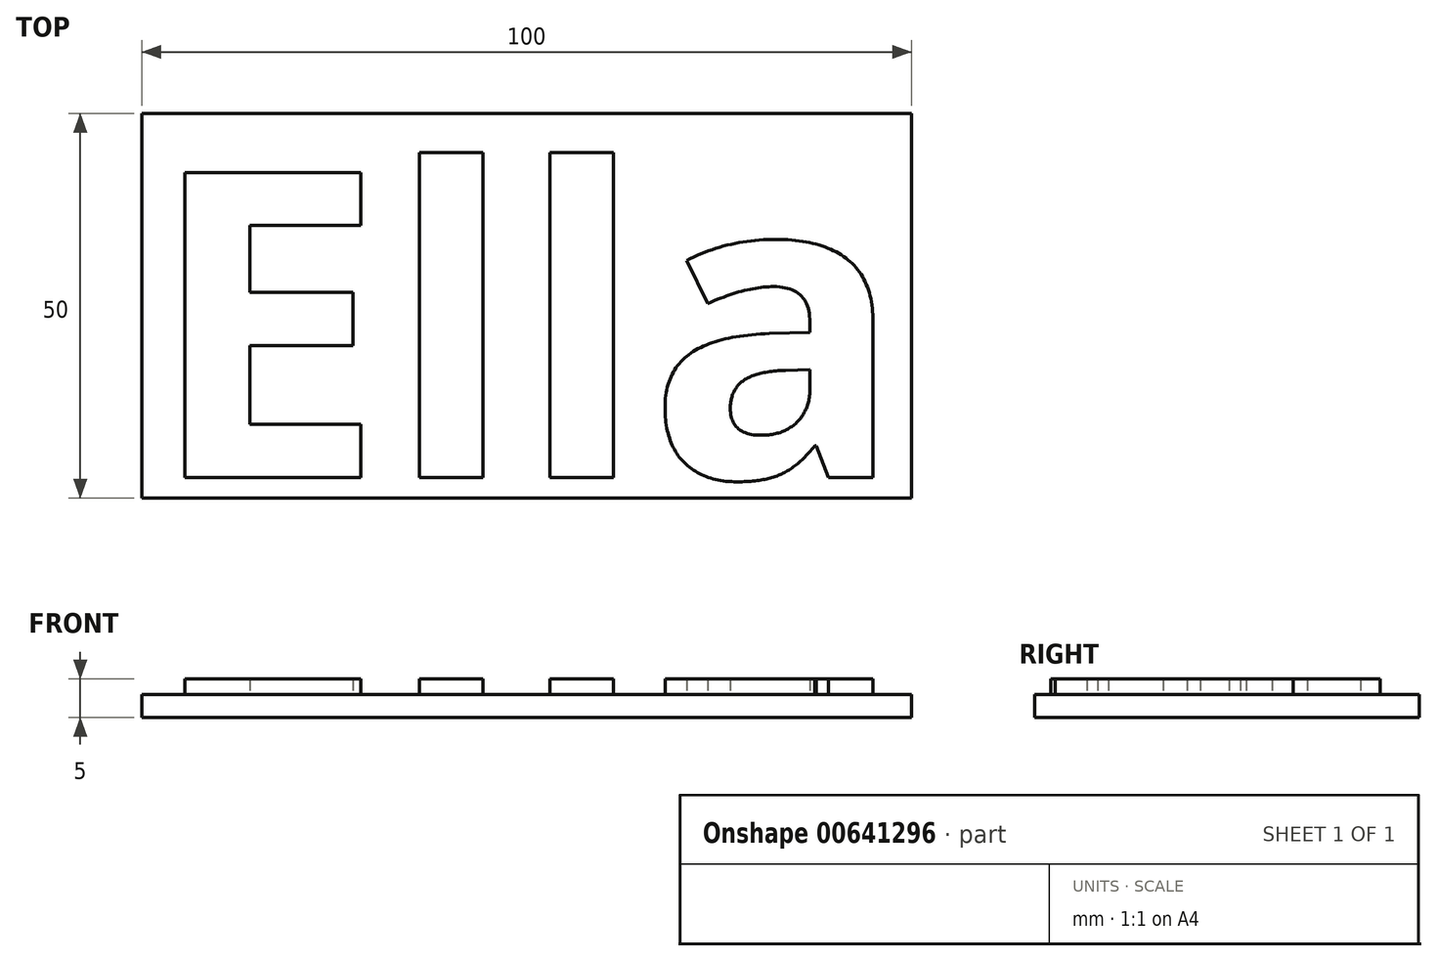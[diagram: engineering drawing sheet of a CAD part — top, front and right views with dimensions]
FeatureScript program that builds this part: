
annotation { "Feature Type Name" : "Feature", "Feature Type Description" : "" }
export const myFeature = defineFeature(function(context is Context, id is Id, definition is map)
    precondition{}
    {
        {
            var Q0;
            Q0=qCreatedBy(makeId("Top.planeOp"),FACE);
            var sketch = newSketch(context, id + "F0", { "sketchPlane" : qUnion([Q0])});
            skLineSegment(sketch, "E0.bottom", {"start": v(0, 0) * mm, "end": v(-100, 0) * mm});
            skLineSegment(sketch, "E0.top", {"start": v(0, 50) * mm, "end": v(-100, 50) * mm});
            skLineSegment(sketch, "E0.left", {"start": v(0, 0) * mm, "end": v(0, 50) * mm});
            skLineSegment(sketch, "E0.right", {"start": v(-100, 0) * mm, "end": v(-100, 50) * mm});
            skSolve(sketch);
        }
        {
            var Q0;
            Q0 = qSketchRegion(id + "F0", true);
            extrude(context, id + "F1", {"entities" : qUnion([Q0]), "depth" : 3 * mm, "offsetDistance" : 25 * mm});
        }
        {
            var Q0;
            Q0=makeQuery(id+"F1.opExtrude","CAP_FACE",FACE,{"disambiguationData":[OSD([sQuery(id+"F0.wireOp",EDGE,"E0.bottom"),sQuery(id+"F0.wireOp",EDGE,"E0.top"),sQuery(id+"F0.wireOp",EDGE,"E0.left"),sQuery(id+"F0.wireOp",EDGE,"E0.right")])],"isStart":false});
            var sketch = newSketch(context, id + "F2", { "sketchPlane" : qUnion([Q0])});
            skText(sketch, "E1", { "text": "Ella", "fontName": "OpenSans-Bold.ttf"});
            const initialGuessF2  = {"E1": [-0.09938, 0.00267, 1, 0, 0.04]};
            skSetInitialGuess(sketch, initialGuessF2);
            skSolve(sketch);
        }
        {
            var Q0;
            Q0 = qSketchRegion(id + "F2", true);
            extrude(context, id + "F3", {"entities" : qUnion([Q0]), "operationType" : NewBodyOperationType.ADD, "depth" : 2 * mm, "offsetDistance" : 25 * mm});
        }
    });
